# Revit family: PD4-C-EN types Avec hôte
name_source: partatom
category: Dispositifs d'éclairage
units: mm (PartAtom-declared; Revit-internal decimal feet)

## family parameters
Conserver l'orientation des annotations = Oui
Cote de connecteur circulaire = Utiliser le diamètre
Couper avec des vides une fois chargée = Non
Hôte = Face
Partagée = Non
Point de calcul de pièce = Non
Type d'élément = Normal

## types (6) — shared parameters
Classe = II
Code d'assemblage = D5010200
Fabricant = B.E.G.
Hauteur de montage max = 280 cm
IP = 20
Image du type = COULOIR.jpg
Marque = LUXOMAT
Mode de pose = Encastré
Température ambiante = -25°C à +50°C
URL = http://www.luxomat.com
zero-valued in all types: Elévation par défaut

## per-type parameters (varying)
| type | Alimentation | Charge Cos ɸ =0.5 | Charge Cos ɸ =1 | Charge LED | Commentaires du type | Consommation | Modèle | Relais | Référence | Type de Sortie |
| 01- PD4-C-EN Générique | 110-240 V AC |  |  |  | DET.PRES.SPECIAL COULOIR.180/360°/2x10M ENCASTRE |  | PD4-C-EN |  |  |  |
| 02- PD4-M-2C-C-EN réf 92443 | 110-240 V AC | 1150 VA | 2300 W | 300 W | DET.PRES.SPECIAL COULOIR.MAITRE.2 CONTACTS.180/360°/2x10M ENCASTRE | 0,47 W | PD4-M-2C-C-EN | 10 A / 3 A | 92443 | TOR + CVC |
| 04- PD4N-KNX-C-DX-EN réf 93389 | 24 V DC par Bus KNX | 0 | 0 | 0 | DET.PRES.SPECIAL COULOIR.KNX.VERSION DELUXE.180/360°/2x10M ENCASTRE | 12 mA | PD4N-KNX-C-DX-EN | 0 | 93389 | KNX - 1 sortie Eclairage TOR ou GRADATION / 3 sorties Présence / Capteur de température et bruit |
| 03- PD4-S-C-EN réf 92445 | 110-240 V AC | 0 | 0 | 0 | DET.PRES.SPECIAL COULOIR.ESCLAVE.180/360°/2x10M ENCASTRE | 0,25 W | PD4-S-C-EN | 0 | 92445 | Esclave |
| 05- PD4N-KNXs-C-ST-EN réf 93515 | 24 V DC par Bus KNX | 0 | 0 | 0 | DET.PRES.SPECIAL COULOIR.KNX Sécure.VERSION STANDARD.180/360°/2x10M ENCASTRE + Lentille Couloir réf 93073 | 12 mA | PD4N-KNXs-C-ST-EN | 0 | 93515+93073 | KNX Sécure - 1 sortie Eclairage TOR ou GRADATION / 3 sorties Présence / HCL |
| 06- PD4N-KNXs-C-DX-EN réf 93517 | 24 V DC par Bus KNX | 0 | 0 | 0 | DET.PRES.SPECIAL COULOIR.KNX Sécure.VERSION DELUXE.180/360°/2x10M ENCASTRE + Lentille Couloir réf 93073 | 12 mA | PD4N-KNXs-C-DX-EN | 0 | 93517+93073 | KNX Sécure - 1 sortie Eclairage TOR ou GRADATION / 3 sorties Présence / Capteur de température et bruit / HCL |
